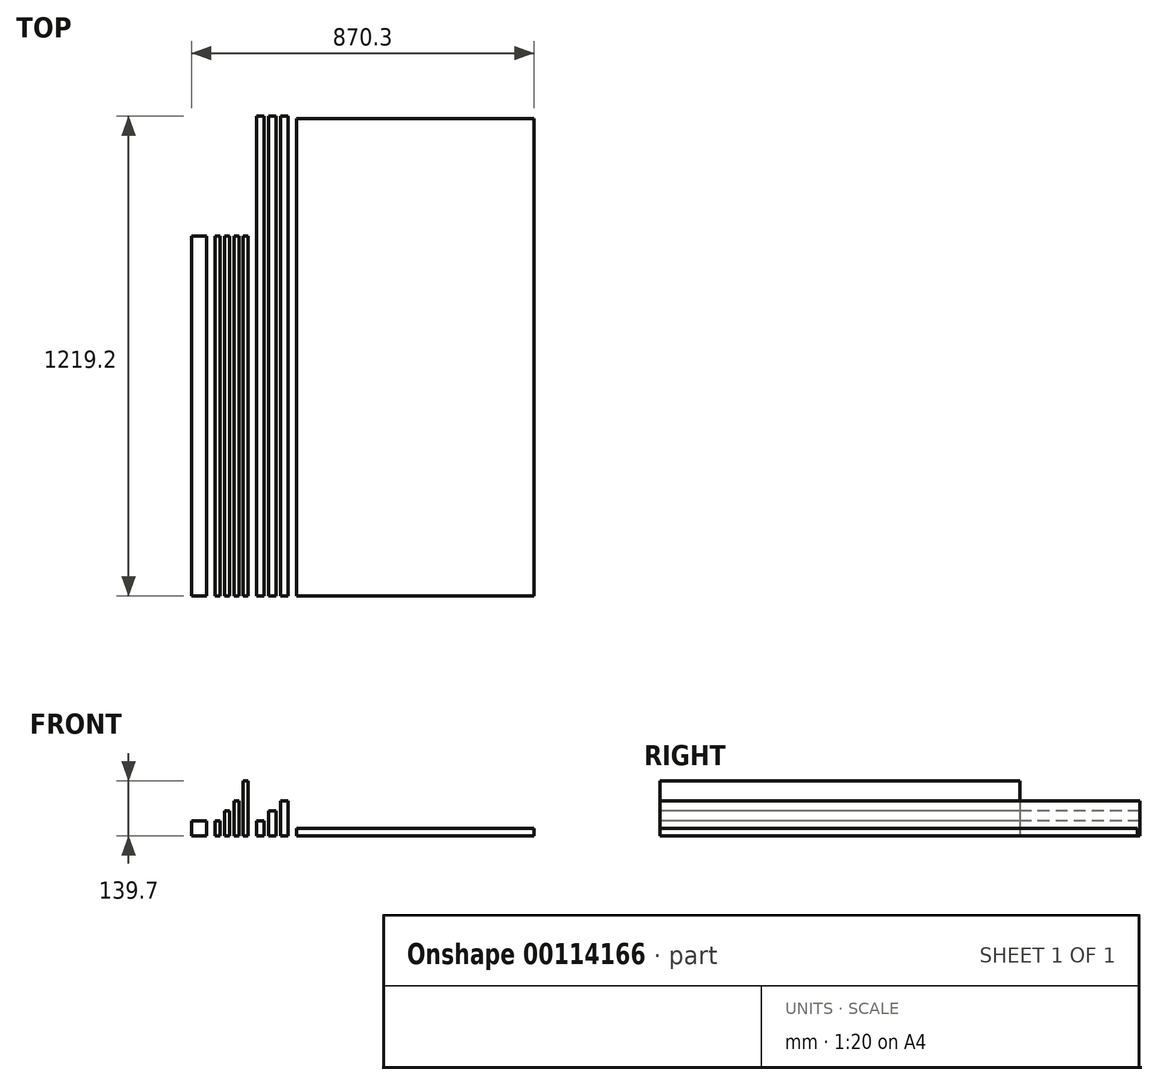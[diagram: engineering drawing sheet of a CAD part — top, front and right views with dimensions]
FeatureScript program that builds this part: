
annotation { "Feature Type Name" : "Feature", "Feature Type Description" : "" }
export const myFeature = defineFeature(function(context is Context, id is Id, definition is map)
    precondition{}
    {
        {
            var Q0;
            Q0=qCreatedBy(makeId("Top.planeOp"),FACE);
            var sketch = newSketch(context, id + "F0", { "sketchPlane" : qUnion([Q0])});
            skLineSegment(sketch, "E0.bottom", {"start": v(0, 1212.85) * mm, "end": v(603.25, 1212.85) * mm});
            skLineSegment(sketch, "E0.top", {"start": v(0, 0) * mm, "end": v(603.25, 0) * mm});
            skLineSegment(sketch, "E0.left", {"start": v(0, 1212.85) * mm, "end": v(0, 0) * mm});
            skLineSegment(sketch, "E0.right", {"start": v(603.25, 1212.85) * mm, "end": v(603.25, 0) * mm});
            skSolve(sketch);
        }
        {
            var Q0;
            Q0=qCreatedBy(makeId("Front.planeOp"),FACE);
            var sketch = newSketch(context, id + "F1", { "sketchPlane" : qUnion([Q0])});
            skLineSegment(sketch, "E1.bottom", {"start": v(-206.95, 38.1) * mm, "end": v(-194.25, 38.1) * mm});
            skLineSegment(sketch, "E1.top", {"start": v(-206.95, 0) * mm, "end": v(-194.25, 0) * mm});
            skLineSegment(sketch, "E1.left", {"start": v(-206.95, 38.1) * mm, "end": v(-206.95, 0) * mm});
            skLineSegment(sketch, "E1.right", {"start": v(-194.25, 38.1) * mm, "end": v(-194.25, 0) * mm});
            skLineSegment(sketch, "E2.bottom", {"start": v(-183.25, 63.5) * mm, "end": v(-170.55, 63.5) * mm});
            skLineSegment(sketch, "E2.top", {"start": v(-183.25, 0) * mm, "end": v(-170.55, 0) * mm});
            skLineSegment(sketch, "E2.left", {"start": v(-183.25, 63.5) * mm, "end": v(-183.25, 0) * mm});
            skLineSegment(sketch, "E2.right", {"start": v(-170.55, 63.5) * mm, "end": v(-170.55, 0) * mm});
            skLineSegment(sketch, "E3.bottom", {"start": v(-159.55, 88.9) * mm, "end": v(-146.85, 88.9) * mm});
            skLineSegment(sketch, "E3.top", {"start": v(-159.55, 0) * mm, "end": v(-146.85, 0) * mm});
            skLineSegment(sketch, "E3.left", {"start": v(-159.55, 88.9) * mm, "end": v(-159.55, 0) * mm});
            skLineSegment(sketch, "E3.right", {"start": v(-146.85, 88.9) * mm, "end": v(-146.85, 0) * mm});
            skLineSegment(sketch, "E4.bottom", {"start": v(-267.05, 38.1) * mm, "end": v(-228.95, 38.1) * mm});
            skLineSegment(sketch, "E4.top", {"start": v(-267.05, 0) * mm, "end": v(-228.95, 0) * mm});
            skLineSegment(sketch, "E4.left", {"start": v(-267.05, 38.1) * mm, "end": v(-267.05, 0) * mm});
            skLineSegment(sketch, "E4.right", {"start": v(-228.95, 38.1) * mm, "end": v(-228.95, 0) * mm});
            skLineSegment(sketch, "E5.bottom", {"start": v(-135.85, 139.7) * mm, "end": v(-123.15, 139.7) * mm});
            skLineSegment(sketch, "E5.top", {"start": v(-135.85, 0) * mm, "end": v(-123.15, 0) * mm});
            skLineSegment(sketch, "E5.left", {"start": v(-135.85, 139.7) * mm, "end": v(-135.85, 0) * mm});
            skLineSegment(sketch, "E5.right", {"start": v(-123.15, 139.7) * mm, "end": v(-123.15, 0) * mm});
            skLineSegment(sketch, "E6.bottom", {"start": v(-101.15, 38.1) * mm, "end": v(-82.1, 38.1) * mm});
            skLineSegment(sketch, "E6.top", {"start": v(-101.15, 0) * mm, "end": v(-82.1, 0) * mm});
            skLineSegment(sketch, "E6.left", {"start": v(-101.15, 38.1) * mm, "end": v(-101.15, 0) * mm});
            skLineSegment(sketch, "E6.right", {"start": v(-82.1, 38.1) * mm, "end": v(-82.1, 0) * mm});
            skLineSegment(sketch, "E7.bottom", {"start": v(-71.1, 63.5) * mm, "end": v(-52.05, 63.5) * mm});
            skLineSegment(sketch, "E7.top", {"start": v(-71.1, 0) * mm, "end": v(-52.05, 0) * mm});
            skLineSegment(sketch, "E7.left", {"start": v(-71.1, 63.5) * mm, "end": v(-71.1, 0) * mm});
            skLineSegment(sketch, "E7.right", {"start": v(-52.05, 63.5) * mm, "end": v(-52.05, 0) * mm});
            skLineSegment(sketch, "E8.bottom", {"start": v(-41.05, 88.9) * mm, "end": v(-22, 88.9) * mm});
            skLineSegment(sketch, "E8.top", {"start": v(-41.05, 0) * mm, "end": v(-22, 0) * mm});
            skLineSegment(sketch, "E8.left", {"start": v(-41.05, 88.9) * mm, "end": v(-41.05, 0) * mm});
            skLineSegment(sketch, "E8.right", {"start": v(-22, 88.9) * mm, "end": v(-22, 0) * mm});
            skLineSegment(sketch, "E9", {"start": v(-300.08, 0) * mm, "end": v(171.99, 0) * mm, "construction": true});
            skLineSegment(sketch, "E10", {"start": v(0, 162.48) * mm, "end": v(0, 0) * mm, "construction": true});
            skSolve(sketch);
        }
        {
            var Q0;
            Q0=makeQuery(id+"F0.imprint","IMPRINT",FACE,{"disambiguationData":[TD([[makeQuery(id+"F0.imprint","IMPRINT",EDGE,{"derivedFrom":sQuery(id+"F0.wireOp",EDGE,"E0.bottom")}),-1.0]])]});
            extrude(context, id + "F2", {"entities" : qUnion([Q0]), "depth" : 18.64 * mm});
        }
        {
            var Q0;
            Q0=makeQuery(id+"F1.imprint","IMPRINT",FACE,{"disambiguationData":[TD([[makeQuery(id+"F1.imprint","IMPRINT",EDGE,{"derivedFrom":sQuery(id+"F1.wireOp",EDGE,"E4.bottom")}),-1.0]])]});
            var Q1;
            Q1=makeQuery(id+"F1.imprint","IMPRINT",FACE,{"disambiguationData":[TD([[makeQuery(id+"F1.imprint","IMPRINT",EDGE,{"derivedFrom":sQuery(id+"F1.wireOp",EDGE,"E1.bottom")}),-1.0]])]});
            var Q2;
            Q2=makeQuery(id+"F1.imprint","IMPRINT",FACE,{"disambiguationData":[TD([[makeQuery(id+"F1.imprint","IMPRINT",EDGE,{"derivedFrom":sQuery(id+"F1.wireOp",EDGE,"E2.bottom")}),-1.0]])]});
            var Q3;
            Q3=makeQuery(id+"F1.imprint","IMPRINT",FACE,{"disambiguationData":[TD([[makeQuery(id+"F1.imprint","IMPRINT",EDGE,{"derivedFrom":sQuery(id+"F1.wireOp",EDGE,"E3.bottom")}),-1.0]])]});
            var Q4;
            Q4=makeQuery(id+"F1.imprint","IMPRINT",FACE,{"disambiguationData":[TD([[makeQuery(id+"F1.imprint","IMPRINT",EDGE,{"derivedFrom":sQuery(id+"F1.wireOp",EDGE,"E5.bottom")}),-1.0]])]});
            extrude(context, id + "F3", {"entities" : qUnion([Q0, Q1, Q2, Q3, Q4]), "oppositeDirection" : true, "depth" : 914.4 * mm});
        }
        {
            var Q0;
            Q0=makeQuery(id+"F1.imprint","IMPRINT",FACE,{"disambiguationData":[TD([[makeQuery(id+"F1.imprint","IMPRINT",EDGE,{"derivedFrom":sQuery(id+"F1.wireOp",EDGE,"E6.bottom")}),-1.0]])]});
            var Q1;
            Q1=makeQuery(id+"F1.imprint","IMPRINT",FACE,{"disambiguationData":[TD([[makeQuery(id+"F1.imprint","IMPRINT",EDGE,{"derivedFrom":sQuery(id+"F1.wireOp",EDGE,"E7.bottom")}),-1.0]])]});
            var Q2;
            Q2=makeQuery(id+"F1.imprint","IMPRINT",FACE,{"disambiguationData":[TD([[makeQuery(id+"F1.imprint","IMPRINT",EDGE,{"derivedFrom":sQuery(id+"F1.wireOp",EDGE,"E8.bottom")}),-1.0]])]});
            extrude(context, id + "F4", {"entities" : qUnion([Q0, Q1, Q2]), "oppositeDirection" : true, "depth" : 1219.2 * mm});
        }
    });
